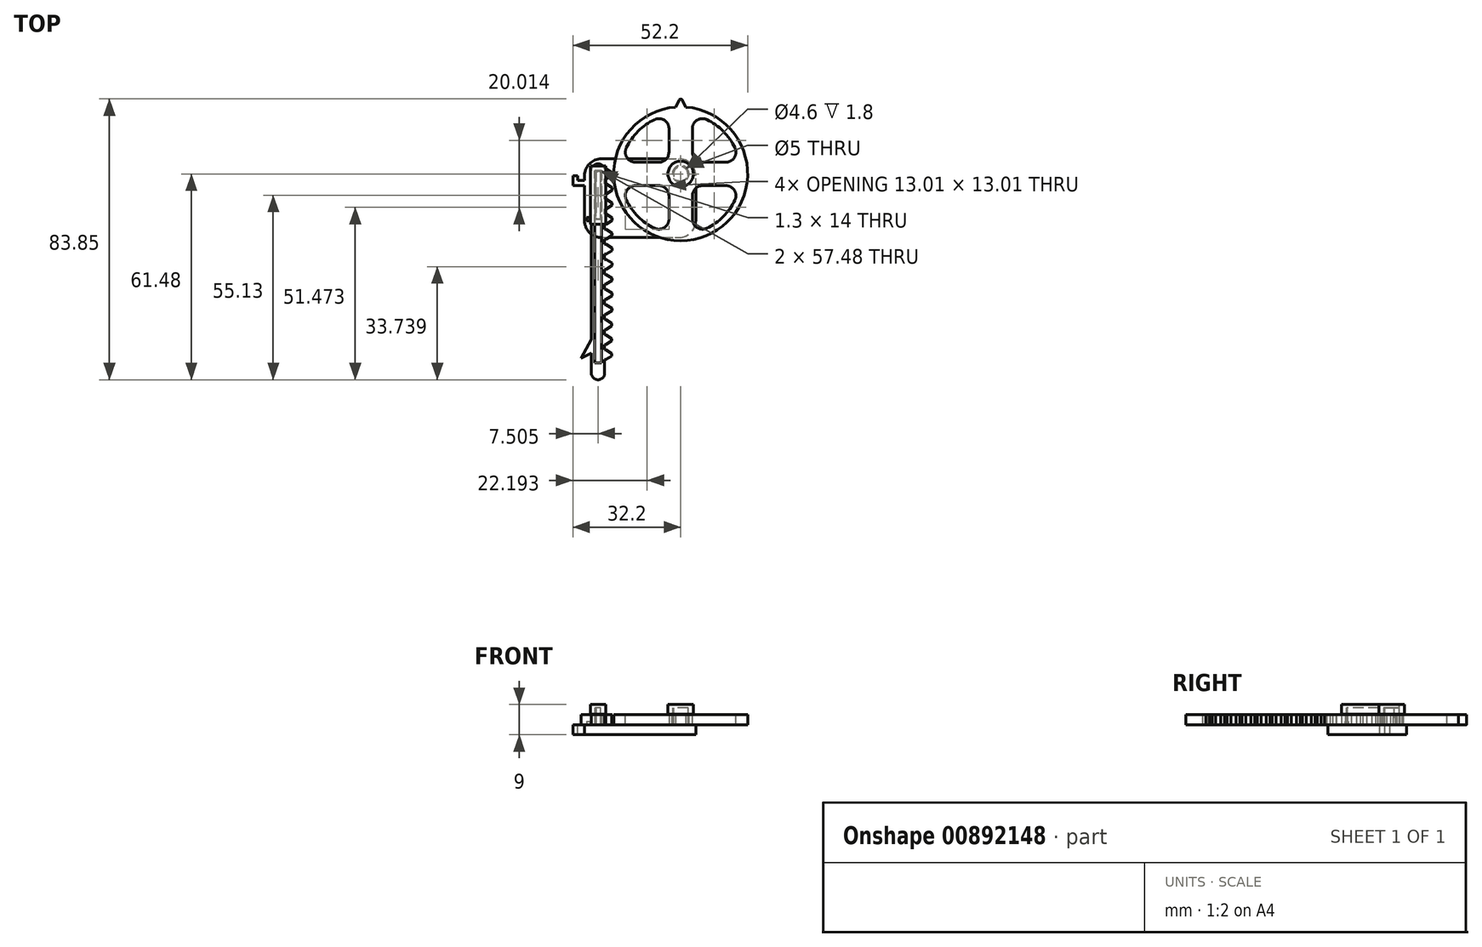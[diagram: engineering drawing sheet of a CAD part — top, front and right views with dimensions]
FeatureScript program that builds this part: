
annotation { "Feature Type Name" : "Feature", "Feature Type Description" : "" }
export const myFeature = defineFeature(function(context is Context, id is Id, definition is map)
    precondition{}
    {
        {
            var Q0;
            Q0=qCreatedBy(makeId("Top.planeOp"),FACE);
            var sketch = newSketch(context, id + "F0", { "sketchPlane" : qUnion([Q0])});
            skCircle(sketch, "E0", {"center": v(0, 0) * mm, "radius": 20 * mm});
            skLineSegment(sketch, "E1", {"start": v(-1.5, 19.94) * mm, "end": v(0, 23) * mm});
            skLineSegment(sketch, "E2", {"start": v(0, 23) * mm, "end": v(1.5, 19.94) * mm});
            skSolve(sketch);
        }
        {
            var Q0;
            {var subQ0=sQuery(id+"F0.wireOp",EDGE,"E0");var subQ1=makeQuery(id+"F0.imprint","INTERSECT",VERTEX,{"derivedFrom":[subQ0,sQuery(id+"F0.wireOp",EDGE,"E1")]});Q0=makeQuery(id+"F0.imprint","IMPRINT",FACE,{"disambiguationData":[TD([[makeQuery(id+"F0.imprint","IMPRINT",EDGE,{"disambiguationData":[TD([[subQ1,1.0]])],"derivedFrom":subQ0}),1.0]])]});}
            extrude(context, id + "F1", {"entities" : qUnion([Q0]), "depth" : 3 * mm, "offsetDistance" : 25 * mm});
        }
        {
            var Q0;
            {var subQ0=sQuery(id+"F0.wireOp",EDGE,"E1");Q0=makeQuery(id+"F0.imprint","IMPRINT",FACE,{"disambiguationData":[TD([[makeQuery(id+"F0.imprint","IMPRINT",EDGE,{"derivedFrom":subQ0}),-1.0]])]});}
            extrude(context, id + "F2", {"entities" : qUnion([Q0]), "operationType" : NewBodyOperationType.ADD, "depth" : 3 * mm, "offsetDistance" : 25 * mm});
        }
        {
            var Q0;
            Q0=makeQuery(id+"F2.opExtrude","SWEPT_EDGE",EDGE,{"disambiguationData":[OSD([sQuery(id+"F0.wireOp",EDGE,"E1"),sQuery(id+"F0.wireOp",EDGE,"E2")])]});
            fillet(context, id + "F3", {"entities" : qUnion([Q0]), "radius" : .5 * mm, "tangentPropagation" : true, "allowEdgeOverflow" : false});
        }
        {
            var Q0;
            Q0=qCreatedBy(makeId("Top.planeOp"),FACE);
            var sketch = newSketch(context, id + "F4", { "sketchPlane" : qUnion([Q0])});
            skLineSegment(sketch, "E3.bottom", {"start": v(-26.7, -61.48) * mm, "end": v(-22.7, -61.48) * mm});
            skLineSegment(sketch, "E3.top", {"start": v(-26.7, 3) * mm, "end": v(-22.7, 3) * mm});
            skLineSegment(sketch, "E3.left", {"start": v(-26.7, -61.48) * mm, "end": v(-26.7, 3) * mm});
            skLineSegment(sketch, "E3.right", {"start": v(-22.7, -61.48) * mm, "end": v(-22.7, 3) * mm});
            skLineSegment(sketch, "E4.117", {"start": v(-22.25, -1.48) * mm, "end": v(-20.45, -0.35) * mm});
            skArc(sketch, "E4.118", {"start": v(-20.45, -0.35) * mm, "mid": v(-20.45, 0) * mm, "end": v(-20.45, 0.35) * mm});
            skLineSegment(sketch, "E4.119", {"start": v(-20.45, 0.35) * mm, "end": v(-22.25, 1.48) * mm});
            skLineSegment(sketch, "E5", {"start": v(-22.25, -1.48) * mm, "end": v(-22.7, -1.48) * mm});
            skLineSegment(sketch, "E6", {"start": v(-22.25, 1.48) * mm, "end": v(-22.7, 1.48) * mm});
            skLineSegment(sketch, "E7.1.0.0", {"start": v(-22.26, -5.98) * mm, "end": v(-22.7, -5.98) * mm});
            skLineSegment(sketch, "E7.1.0.1", {"start": v(-20.46, -4.15) * mm, "end": v(-22.26, -3.02) * mm});
            skArc(sketch, "E7.1.0.2", {"start": v(-20.46, -4.85) * mm, "mid": v(-20.46, -4.5) * mm, "end": v(-20.46, -4.15) * mm});
            skLineSegment(sketch, "E7.1.0.3", {"start": v(-22.26, -3.02) * mm, "end": v(-22.7, -3.02) * mm});
            skLineSegment(sketch, "E7.1.0.4", {"start": v(-22.26, -5.98) * mm, "end": v(-20.46, -4.85) * mm});
            skLineSegment(sketch, "E7.2.0.0", {"start": v(-22.27, -10.48) * mm, "end": v(-22.71, -10.48) * mm});
            skLineSegment(sketch, "E7.2.0.1", {"start": v(-20.46, -8.65) * mm, "end": v(-22.27, -7.52) * mm});
            skArc(sketch, "E7.2.0.2", {"start": v(-20.46, -9.35) * mm, "mid": v(-20.47, -9) * mm, "end": v(-20.46, -8.65) * mm});
            skLineSegment(sketch, "E7.2.0.3", {"start": v(-22.27, -7.52) * mm, "end": v(-22.71, -7.52) * mm});
            skLineSegment(sketch, "E7.2.0.4", {"start": v(-22.27, -10.48) * mm, "end": v(-20.46, -9.35) * mm});
            skLineSegment(sketch, "E7.3.0.0", {"start": v(-22.27, -14.98) * mm, "end": v(-22.72, -14.98) * mm});
            skLineSegment(sketch, "E7.3.0.1", {"start": v(-20.47, -13.15) * mm, "end": v(-22.27, -12.02) * mm});
            skArc(sketch, "E7.3.0.2", {"start": v(-20.47, -13.85) * mm, "mid": v(-20.47, -13.5) * mm, "end": v(-20.47, -13.15) * mm});
            skLineSegment(sketch, "E7.3.0.3", {"start": v(-22.27, -12.02) * mm, "end": v(-22.72, -12.02) * mm});
            skLineSegment(sketch, "E7.3.0.4", {"start": v(-22.27, -14.98) * mm, "end": v(-20.47, -13.85) * mm});
            skLineSegment(sketch, "E7.4.0.0", {"start": v(-22.28, -19.48) * mm, "end": v(-22.73, -19.48) * mm});
            skLineSegment(sketch, "E7.4.0.1", {"start": v(-20.48, -17.65) * mm, "end": v(-22.28, -16.52) * mm});
            skArc(sketch, "E7.4.0.2", {"start": v(-20.48, -18.35) * mm, "mid": v(-20.48, -18) * mm, "end": v(-20.48, -17.65) * mm});
            skLineSegment(sketch, "E7.4.0.3", {"start": v(-22.28, -16.52) * mm, "end": v(-22.73, -16.52) * mm});
            skLineSegment(sketch, "E7.4.0.4", {"start": v(-22.28, -19.48) * mm, "end": v(-20.48, -18.35) * mm});
            skLineSegment(sketch, "E7.5.0.0", {"start": v(-22.3, -23.98) * mm, "end": v(-22.74, -23.98) * mm});
            skLineSegment(sketch, "E7.5.0.1", {"start": v(-20.49, -22.15) * mm, "end": v(-22.3, -21.02) * mm});
            skArc(sketch, "E7.5.0.2", {"start": v(-20.49, -22.85) * mm, "mid": v(-20.5, -22.5) * mm, "end": v(-20.49, -22.15) * mm});
            skLineSegment(sketch, "E7.5.0.3", {"start": v(-22.3, -21.02) * mm, "end": v(-22.74, -21.02) * mm});
            skLineSegment(sketch, "E7.5.0.4", {"start": v(-22.3, -23.98) * mm, "end": v(-20.49, -22.85) * mm});
            skLineSegment(sketch, "E7.6.0.0", {"start": v(-22.3, -28.48) * mm, "end": v(-22.74, -28.48) * mm});
            skLineSegment(sketch, "E7.6.0.1", {"start": v(-20.5, -26.65) * mm, "end": v(-22.3, -25.52) * mm});
            skArc(sketch, "E7.6.0.2", {"start": v(-20.5, -27.35) * mm, "mid": v(-20.5, -27) * mm, "end": v(-20.5, -26.65) * mm});
            skLineSegment(sketch, "E7.6.0.3", {"start": v(-22.3, -25.52) * mm, "end": v(-22.74, -25.52) * mm});
            skLineSegment(sketch, "E7.6.0.4", {"start": v(-22.3, -28.48) * mm, "end": v(-20.5, -27.35) * mm});
            skLineSegment(sketch, "E7.7.0.0", {"start": v(-22.3, -32.98) * mm, "end": v(-22.75, -32.98) * mm});
            skLineSegment(sketch, "E7.7.0.1", {"start": v(-20.5, -31.15) * mm, "end": v(-22.3, -30.02) * mm});
            skArc(sketch, "E7.7.0.2", {"start": v(-20.5, -31.85) * mm, "mid": v(-20.5, -31.5) * mm, "end": v(-20.5, -31.15) * mm});
            skLineSegment(sketch, "E7.7.0.3", {"start": v(-22.3, -30.02) * mm, "end": v(-22.75, -30.02) * mm});
            skLineSegment(sketch, "E7.7.0.4", {"start": v(-22.3, -32.98) * mm, "end": v(-20.5, -31.85) * mm});
            skLineSegment(sketch, "E7.8.0.0", {"start": v(-22.32, -37.48) * mm, "end": v(-22.76, -37.48) * mm});
            skLineSegment(sketch, "E7.8.0.1", {"start": v(-20.51, -35.65) * mm, "end": v(-22.32, -34.52) * mm});
            skArc(sketch, "E7.8.0.2", {"start": v(-20.51, -36.35) * mm, "mid": v(-20.51, -36) * mm, "end": v(-20.51, -35.65) * mm});
            skLineSegment(sketch, "E7.8.0.3", {"start": v(-22.32, -34.52) * mm, "end": v(-22.76, -34.52) * mm});
            skLineSegment(sketch, "E7.8.0.4", {"start": v(-22.32, -37.48) * mm, "end": v(-20.51, -36.35) * mm});
            skLineSegment(sketch, "E7.9.0.0", {"start": v(-22.32, -41.98) * mm, "end": v(-22.77, -41.98) * mm});
            skLineSegment(sketch, "E7.9.0.1", {"start": v(-20.52, -40.15) * mm, "end": v(-22.32, -39.02) * mm});
            skArc(sketch, "E7.9.0.2", {"start": v(-20.52, -40.85) * mm, "mid": v(-20.52, -40.5) * mm, "end": v(-20.52, -40.15) * mm});
            skLineSegment(sketch, "E7.9.0.3", {"start": v(-22.32, -39.02) * mm, "end": v(-22.77, -39.02) * mm});
            skLineSegment(sketch, "E7.9.0.4", {"start": v(-22.32, -41.98) * mm, "end": v(-20.52, -40.85) * mm});
            skLineSegment(sketch, "E7.10.0.0", {"start": v(-22.33, -46.48) * mm, "end": v(-22.78, -46.48) * mm});
            skLineSegment(sketch, "E7.10.0.1", {"start": v(-20.53, -44.65) * mm, "end": v(-22.33, -43.52) * mm});
            skArc(sketch, "E7.10.0.2", {"start": v(-20.53, -45.35) * mm, "mid": v(-20.53, -45) * mm, "end": v(-20.53, -44.65) * mm});
            skLineSegment(sketch, "E7.10.0.3", {"start": v(-22.33, -43.52) * mm, "end": v(-22.78, -43.52) * mm});
            skLineSegment(sketch, "E7.10.0.4", {"start": v(-22.33, -46.48) * mm, "end": v(-20.53, -45.35) * mm});
            skLineSegment(sketch, "E7.11.0.0", {"start": v(-22.34, -50.98) * mm, "end": v(-22.78, -50.98) * mm});
            skLineSegment(sketch, "E7.11.0.1", {"start": v(-20.54, -49.15) * mm, "end": v(-22.34, -48.02) * mm});
            skArc(sketch, "E7.11.0.2", {"start": v(-20.54, -49.85) * mm, "mid": v(-20.54, -49.5) * mm, "end": v(-20.54, -49.15) * mm});
            skLineSegment(sketch, "E7.11.0.3", {"start": v(-22.34, -48.02) * mm, "end": v(-22.78, -48.02) * mm});
            skLineSegment(sketch, "E7.11.0.4", {"start": v(-22.34, -50.98) * mm, "end": v(-20.54, -49.85) * mm});
            skLineSegment(sketch, "E7.12.0.0", {"start": v(-22.35, -55.48) * mm, "end": v(-22.8, -55.48) * mm});
            skLineSegment(sketch, "E7.12.0.1", {"start": v(-20.54, -53.65) * mm, "end": v(-22.35, -52.52) * mm});
            skArc(sketch, "E7.12.0.2", {"start": v(-20.54, -54.35) * mm, "mid": v(-20.55, -54) * mm, "end": v(-20.54, -53.65) * mm});
            skLineSegment(sketch, "E7.12.0.3", {"start": v(-22.35, -52.52) * mm, "end": v(-22.8, -52.52) * mm});
            skLineSegment(sketch, "E7.12.0.4", {"start": v(-22.35, -55.48) * mm, "end": v(-20.54, -54.35) * mm});
            skLineSegment(sketch, "E7.direction1", {"start": v(-22.7, -1.48) * mm, "end": v(-22.7, -5.98) * mm, "construction": true});
            skSolve(sketch);
        }
        {
            var Q0;
            Q0 = qSketchRegion(id + "F4", true);
            extrude(context, id + "F5", {"entities" : qUnion([Q0]), "depth" : 3 * mm, "offsetDistance" : 25 * mm});
        }
        {
            var Q0;
            Q0=makeQuery(id+"F5.opExtrude","CAP_FACE",FACE,{"disambiguationData":[OSD([sQuery(id+"F4.wireOp",EDGE,"E3.bottom"),sQuery(id+"F4.wireOp",EDGE,"E3.top"),sQuery(id+"F4.wireOp",EDGE,"E3.left"),sQuery(id+"F4.wireOp",EDGE,"E3.right"),sQuery(id+"F4.wireOp",EDGE,"E4.117"),sQuery(id+"F4.wireOp",EDGE,"E4.118"),sQuery(id+"F4.wireOp",EDGE,"E4.119"),sQuery(id+"F4.wireOp",EDGE,"E5"),sQuery(id+"F4.wireOp",EDGE,"E6"),sQuery(id+"F4.wireOp",EDGE,"E7.1.0.0"),sQuery(id+"F4.wireOp",EDGE,"E7.1.0.1"),sQuery(id+"F4.wireOp",EDGE,"E7.1.0.2"),sQuery(id+"F4.wireOp",EDGE,"E7.1.0.3"),sQuery(id+"F4.wireOp",EDGE,"E7.1.0.4"),sQuery(id+"F4.wireOp",EDGE,"E7.2.0.0"),sQuery(id+"F4.wireOp",EDGE,"E7.2.0.1"),sQuery(id+"F4.wireOp",EDGE,"E7.2.0.2"),sQuery(id+"F4.wireOp",EDGE,"E7.2.0.3"),sQuery(id+"F4.wireOp",EDGE,"E7.2.0.4"),sQuery(id+"F4.wireOp",EDGE,"E7.3.0.0"),sQuery(id+"F4.wireOp",EDGE,"E7.3.0.1"),sQuery(id+"F4.wireOp",EDGE,"E7.3.0.2"),sQuery(id+"F4.wireOp",EDGE,"E7.3.0.3"),sQuery(id+"F4.wireOp",EDGE,"E7.3.0.4"),sQuery(id+"F4.wireOp",EDGE,"E7.4.0.0"),sQuery(id+"F4.wireOp",EDGE,"E7.4.0.1"),sQuery(id+"F4.wireOp",EDGE,"E7.4.0.2"),sQuery(id+"F4.wireOp",EDGE,"E7.4.0.3"),sQuery(id+"F4.wireOp",EDGE,"E7.4.0.4"),sQuery(id+"F4.wireOp",EDGE,"E7.5.0.0"),sQuery(id+"F4.wireOp",EDGE,"E7.5.0.1"),sQuery(id+"F4.wireOp",EDGE,"E7.5.0.2"),sQuery(id+"F4.wireOp",EDGE,"E7.5.0.3"),sQuery(id+"F4.wireOp",EDGE,"E7.5.0.4"),sQuery(id+"F4.wireOp",EDGE,"E7.6.0.0"),sQuery(id+"F4.wireOp",EDGE,"E7.6.0.1"),sQuery(id+"F4.wireOp",EDGE,"E7.6.0.2"),sQuery(id+"F4.wireOp",EDGE,"E7.6.0.3"),sQuery(id+"F4.wireOp",EDGE,"E7.6.0.4"),sQuery(id+"F4.wireOp",EDGE,"E7.7.0.0"),sQuery(id+"F4.wireOp",EDGE,"E7.7.0.1"),sQuery(id+"F4.wireOp",EDGE,"E7.7.0.2"),sQuery(id+"F4.wireOp",EDGE,"E7.7.0.3"),sQuery(id+"F4.wireOp",EDGE,"E7.7.0.4"),sQuery(id+"F4.wireOp",EDGE,"E7.8.0.0"),sQuery(id+"F4.wireOp",EDGE,"E7.8.0.1"),sQuery(id+"F4.wireOp",EDGE,"E7.8.0.2"),sQuery(id+"F4.wireOp",EDGE,"E7.8.0.3"),sQuery(id+"F4.wireOp",EDGE,"E7.8.0.4"),sQuery(id+"F4.wireOp",EDGE,"E7.9.0.0"),sQuery(id+"F4.wireOp",EDGE,"E7.9.0.1"),sQuery(id+"F4.wireOp",EDGE,"E7.9.0.2"),sQuery(id+"F4.wireOp",EDGE,"E7.9.0.3"),sQuery(id+"F4.wireOp",EDGE,"E7.9.0.4"),sQuery(id+"F4.wireOp",EDGE,"E7.10.0.0"),sQuery(id+"F4.wireOp",EDGE,"E7.10.0.1"),sQuery(id+"F4.wireOp",EDGE,"E7.10.0.2"),sQuery(id+"F4.wireOp",EDGE,"E7.10.0.3"),sQuery(id+"F4.wireOp",EDGE,"E7.10.0.4"),sQuery(id+"F4.wireOp",EDGE,"E7.11.0.0"),sQuery(id+"F4.wireOp",EDGE,"E7.11.0.1"),sQuery(id+"F4.wireOp",EDGE,"E7.11.0.2"),sQuery(id+"F4.wireOp",EDGE,"E7.11.0.3"),sQuery(id+"F4.wireOp",EDGE,"E7.11.0.4"),sQuery(id+"F4.wireOp",EDGE,"E7.12.0.0"),sQuery(id+"F4.wireOp",EDGE,"E7.12.0.1"),sQuery(id+"F4.wireOp",EDGE,"E7.12.0.2"),sQuery(id+"F4.wireOp",EDGE,"E7.12.0.3"),sQuery(id+"F4.wireOp",EDGE,"E7.12.0.4")])],"isStart":true});
            var sketch = newSketch(context, id + "F6", { "sketchPlane" : qUnion([Q0])});
            skLineSegment(sketch, "E8.bottom", {"start": v(-25.7, 56.48) * mm, "end": v(-23.7, 56.48) * mm});
            skLineSegment(sketch, "E8.top", {"start": v(-25.7, -1) * mm, "end": v(-23.7, -1) * mm});
            skLineSegment(sketch, "E8.left", {"start": v(-25.7, 56.48) * mm, "end": v(-25.7, -1) * mm});
            skLineSegment(sketch, "E8.right", {"start": v(-23.7, 56.48) * mm, "end": v(-23.7, -1) * mm});
            skSolve(sketch);
        }
        {
            var Q0;
            Q0=makeQuery(id+"F6.imprint","IMPRINT",FACE,{"disambiguationData":[TD([[makeQuery(id+"F6.imprint","IMPRINT",EDGE,{"derivedFrom":sQuery(id+"F6.wireOp",EDGE,"E8.bottom")}),-1.0]])]});
            extrude(context, id + "F7", {"entities" : qUnion([Q0]), "operationType" : NewBodyOperationType.REMOVE, "endBound" : BoundingType.THROUGH_ALL, "oppositeDirection" : true, "depth" : 25 * mm, "offsetDistance" : 25 * mm});
        }
        {
            var Q0;
            Q0=makeQuery(id+"F5.opExtrude","SWEPT_EDGE",EDGE,{"disambiguationData":[OSD([sQuery(id+"F4.wireOp",EDGE,"E3.top"),sQuery(id+"F4.wireOp",EDGE,"E3.right")])]});
            var Q1;
            Q1=makeQuery(id+"F5.opExtrude","SWEPT_EDGE",EDGE,{"disambiguationData":[OSD([sQuery(id+"F4.wireOp",EDGE,"E3.top"),sQuery(id+"F4.wireOp",EDGE,"E3.left")])]});
            var Q2;
            Q2=makeQuery(id+"F5.opExtrude","SWEPT_EDGE",EDGE,{"disambiguationData":[OSD([sQuery(id+"F4.wireOp",EDGE,"E3.bottom"),sQuery(id+"F4.wireOp",EDGE,"E3.left")])]});
            var Q3;
            Q3=makeQuery(id+"F5.opExtrude","SWEPT_EDGE",EDGE,{"disambiguationData":[OSD([sQuery(id+"F4.wireOp",EDGE,"E3.bottom"),sQuery(id+"F4.wireOp",EDGE,"E3.right")])]});
            fillet(context, id + "F8", {"entities" : qUnion([Q0, Q1, Q2, Q3]), "radius" : 2 * mm, "tangentPropagation" : true, "allowEdgeOverflow" : false});
        }
        {
            var Q0;
            {var subQ0=sQuery(id+"F0.wireOp",EDGE,"E2");var subQ1=sQuery(id+"F0.wireOp",EDGE,"E1");var subQ2=sQuery(id+"F0.wireOp",EDGE,"E0");Q0=makeQuery(id+"FbRMCi4XYvqGRgo_1.29.F2.boolean.opBoolean","MERGE",FACE,{"derivedFrom":[makeQuery(id+"FbRMCi4XYvqGRgo_1.28.F2.boolean.opBoolean","MERGE",FACE,{"derivedFrom":[makeQuery(id+"FbRMCi4XYvqGRgo_1.27.F2.boolean.opBoolean","MERGE",FACE,{"derivedFrom":[makeQuery(id+"FbRMCi4XYvqGRgo_1.26.F2.boolean.opBoolean","MERGE",FACE,{"derivedFrom":[makeQuery(id+"FbRMCi4XYvqGRgo_1.25.F2.boolean.opBoolean","MERGE",FACE,{"derivedFrom":[makeQuery(id+"FbRMCi4XYvqGRgo_1.24.F2.boolean.opBoolean","MERGE",FACE,{"derivedFrom":[makeQuery(id+"FbRMCi4XYvqGRgo_1.23.F2.boolean.opBoolean","MERGE",FACE,{"derivedFrom":[makeQuery(id+"FbRMCi4XYvqGRgo_1.22.F2.boolean.opBoolean","MERGE",FACE,{"derivedFrom":[makeQuery(id+"FbRMCi4XYvqGRgo_1.21.F2.boolean.opBoolean","MERGE",FACE,{"derivedFrom":[makeQuery(id+"FbRMCi4XYvqGRgo_1.20.F2.boolean.opBoolean","MERGE",FACE,{"derivedFrom":[makeQuery(id+"FbRMCi4XYvqGRgo_1.19.F2.boolean.opBoolean","MERGE",FACE,{"derivedFrom":[makeQuery(id+"FbRMCi4XYvqGRgo_1.18.F2.boolean.opBoolean","MERGE",FACE,{"derivedFrom":[makeQuery(id+"FbRMCi4XYvqGRgo_1.17.F2.boolean.opBoolean","MERGE",FACE,{"derivedFrom":[makeQuery(id+"FbRMCi4XYvqGRgo_1.16.F2.boolean.opBoolean","MERGE",FACE,{"derivedFrom":[makeQuery(id+"FbRMCi4XYvqGRgo_1.15.F2.boolean.opBoolean","MERGE",FACE,{"derivedFrom":[makeQuery(id+"FbRMCi4XYvqGRgo_1.14.F2.boolean.opBoolean","MERGE",FACE,{"derivedFrom":[makeQuery(id+"FbRMCi4XYvqGRgo_1.13.F2.boolean.opBoolean","MERGE",FACE,{"derivedFrom":[makeQuery(id+"FbRMCi4XYvqGRgo_1.12.F2.boolean.opBoolean","MERGE",FACE,{"derivedFrom":[makeQuery(id+"FbRMCi4XYvqGRgo_1.11.F2.boolean.opBoolean","MERGE",FACE,{"derivedFrom":[makeQuery(id+"FbRMCi4XYvqGRgo_1.10.F2.boolean.opBoolean","MERGE",FACE,{"derivedFrom":[makeQuery(id+"FbRMCi4XYvqGRgo_1.9.F2.boolean.opBoolean","MERGE",FACE,{"derivedFrom":[makeQuery(id+"FbRMCi4XYvqGRgo_1.8.F2.boolean.opBoolean","MERGE",FACE,{"derivedFrom":[makeQuery(id+"FbRMCi4XYvqGRgo_1.7.F2.boolean.opBoolean","MERGE",FACE,{"derivedFrom":[makeQuery(id+"FbRMCi4XYvqGRgo_1.6.F2.boolean.opBoolean","MERGE",FACE,{"derivedFrom":[makeQuery(id+"FbRMCi4XYvqGRgo_1.5.F2.boolean.opBoolean","MERGE",FACE,{"derivedFrom":[makeQuery(id+"FbRMCi4XYvqGRgo_1.4.F2.boolean.opBoolean","MERGE",FACE,{"derivedFrom":[makeQuery(id+"FbRMCi4XYvqGRgo_1.3.F2.boolean.opBoolean","MERGE",FACE,{"derivedFrom":[makeQuery(id+"FbRMCi4XYvqGRgo_1.2.F2.boolean.opBoolean","MERGE",FACE,{"derivedFrom":[makeQuery(id+"FbRMCi4XYvqGRgo_1.1.F2.boolean.opBoolean","MERGE",FACE,{"derivedFrom":[makeQuery(id+"F2.boolean.opBoolean","MERGE",FACE,{"derivedFrom":[makeQuery(id+"F1.opExtrude","CAP_FACE",FACE,{"disambiguationData":[OSD([subQ2])],"isStart":false}),makeQuery(id+"F2.opExtrude","CAP_FACE",FACE,{"disambiguationData":[OSD([subQ2,subQ1,subQ0])],"isStart":false})]}),makeQuery(id+"FbRMCi4XYvqGRgo_1.1.F2.opExtrude","CAP_FACE",FACE,{"disambiguationData":[OSD([subQ2,subQ1,subQ0])],"isStart":false})]}),makeQuery(id+"FbRMCi4XYvqGRgo_1.2.F2.opExtrude","CAP_FACE",FACE,{"disambiguationData":[OSD([subQ2,subQ1,subQ0])],"isStart":false})]}),makeQuery(id+"FbRMCi4XYvqGRgo_1.3.F2.opExtrude","CAP_FACE",FACE,{"disambiguationData":[OSD([subQ2,subQ1,subQ0])],"isStart":false})]}),makeQuery(id+"FbRMCi4XYvqGRgo_1.4.F2.opExtrude","CAP_FACE",FACE,{"disambiguationData":[OSD([subQ2,subQ1,subQ0])],"isStart":false})]}),makeQuery(id+"FbRMCi4XYvqGRgo_1.5.F2.opExtrude","CAP_FACE",FACE,{"disambiguationData":[OSD([subQ2,subQ1,subQ0])],"isStart":false})]}),makeQuery(id+"FbRMCi4XYvqGRgo_1.6.F2.opExtrude","CAP_FACE",FACE,{"disambiguationData":[OSD([subQ2,subQ1,subQ0])],"isStart":false})]}),makeQuery(id+"FbRMCi4XYvqGRgo_1.7.F2.opExtrude","CAP_FACE",FACE,{"disambiguationData":[OSD([subQ2,subQ1,subQ0])],"isStart":false})]}),makeQuery(id+"FbRMCi4XYvqGRgo_1.8.F2.opExtrude","CAP_FACE",FACE,{"disambiguationData":[OSD([subQ2,subQ1,subQ0])],"isStart":false})]}),makeQuery(id+"FbRMCi4XYvqGRgo_1.9.F2.opExtrude","CAP_FACE",FACE,{"disambiguationData":[OSD([subQ2,subQ1,subQ0])],"isStart":false})]}),makeQuery(id+"FbRMCi4XYvqGRgo_1.10.F2.opExtrude","CAP_FACE",FACE,{"disambiguationData":[OSD([subQ2,subQ1,subQ0])],"isStart":false})]}),makeQuery(id+"FbRMCi4XYvqGRgo_1.11.F2.opExtrude","CAP_FACE",FACE,{"disambiguationData":[OSD([subQ2,subQ1,subQ0])],"isStart":false})]}),makeQuery(id+"FbRMCi4XYvqGRgo_1.12.F2.opExtrude","CAP_FACE",FACE,{"disambiguationData":[OSD([subQ2,subQ1,subQ0])],"isStart":false})]}),makeQuery(id+"FbRMCi4XYvqGRgo_1.13.F2.opExtrude","CAP_FACE",FACE,{"disambiguationData":[OSD([subQ2,subQ1,subQ0])],"isStart":false})]}),makeQuery(id+"FbRMCi4XYvqGRgo_1.14.F2.opExtrude","CAP_FACE",FACE,{"disambiguationData":[OSD([subQ2,subQ1,subQ0])],"isStart":false})]}),makeQuery(id+"FbRMCi4XYvqGRgo_1.15.F2.opExtrude","CAP_FACE",FACE,{"disambiguationData":[OSD([subQ2,subQ1,subQ0])],"isStart":false})]}),makeQuery(id+"FbRMCi4XYvqGRgo_1.16.F2.opExtrude","CAP_FACE",FACE,{"disambiguationData":[OSD([subQ2,subQ1,subQ0])],"isStart":false})]}),makeQuery(id+"FbRMCi4XYvqGRgo_1.17.F2.opExtrude","CAP_FACE",FACE,{"disambiguationData":[OSD([subQ2,subQ1,subQ0])],"isStart":false})]}),makeQuery(id+"FbRMCi4XYvqGRgo_1.18.F2.opExtrude","CAP_FACE",FACE,{"disambiguationData":[OSD([subQ2,subQ1,subQ0])],"isStart":false})]}),makeQuery(id+"FbRMCi4XYvqGRgo_1.19.F2.opExtrude","CAP_FACE",FACE,{"disambiguationData":[OSD([subQ2,subQ1,subQ0])],"isStart":false})]}),makeQuery(id+"FbRMCi4XYvqGRgo_1.20.F2.opExtrude","CAP_FACE",FACE,{"disambiguationData":[OSD([subQ2,subQ1,subQ0])],"isStart":false})]}),makeQuery(id+"FbRMCi4XYvqGRgo_1.21.F2.opExtrude","CAP_FACE",FACE,{"disambiguationData":[OSD([subQ2,subQ1,subQ0])],"isStart":false})]}),makeQuery(id+"FbRMCi4XYvqGRgo_1.22.F2.opExtrude","CAP_FACE",FACE,{"disambiguationData":[OSD([subQ2,subQ1,subQ0])],"isStart":false})]}),makeQuery(id+"FbRMCi4XYvqGRgo_1.23.F2.opExtrude","CAP_FACE",FACE,{"disambiguationData":[OSD([subQ2,subQ1,subQ0])],"isStart":false})]}),makeQuery(id+"FbRMCi4XYvqGRgo_1.24.F2.opExtrude","CAP_FACE",FACE,{"disambiguationData":[OSD([subQ2,subQ1,subQ0])],"isStart":false})]}),makeQuery(id+"FbRMCi4XYvqGRgo_1.25.F2.opExtrude","CAP_FACE",FACE,{"disambiguationData":[OSD([subQ2,subQ1,subQ0])],"isStart":false})]}),makeQuery(id+"FbRMCi4XYvqGRgo_1.26.F2.opExtrude","CAP_FACE",FACE,{"disambiguationData":[OSD([subQ2,subQ1,subQ0])],"isStart":false})]}),makeQuery(id+"FbRMCi4XYvqGRgo_1.27.F2.opExtrude","CAP_FACE",FACE,{"disambiguationData":[OSD([subQ2,subQ1,subQ0])],"isStart":false})]}),makeQuery(id+"FbRMCi4XYvqGRgo_1.28.F2.opExtrude","CAP_FACE",FACE,{"disambiguationData":[OSD([subQ2,subQ1,subQ0])],"isStart":false})]}),makeQuery(id+"FbRMCi4XYvqGRgo_1.29.F2.opExtrude","CAP_FACE",FACE,{"disambiguationData":[OSD([subQ2,subQ1,subQ0])],"isStart":false})]});}
            var sketch = newSketch(context, id + "F9", { "sketchPlane" : qUnion([Q0])});
            skCircle(sketch, "E9", {"center": v(0, 0) * mm, "radius": 18 * mm});
            skSolve(sketch);
        }
        {
            var Q0;
            Q0=makeQuery(id+"F9.imprint","IMPRINT",FACE,{"disambiguationData":[TD([[makeQuery(id+"F9.imprint","IMPRINT",EDGE,{"derivedFrom":sQuery(id+"F9.wireOp",EDGE,"E9")}),1.0]])]});
            extrude(context, id + "F10", {"entities" : qUnion([Q0]), "operationType" : NewBodyOperationType.REMOVE, "endBound" : BoundingType.THROUGH_ALL, "oppositeDirection" : true, "depth" : 25 * mm, "offsetDistance" : 25 * mm});
        }
        {
            var Q0;
            Q0=qCreatedBy(makeId("Top.planeOp"),FACE);
            var sketch = newSketch(context, id + "F11", { "sketchPlane" : qUnion([Q0])});
            skLineSegment(sketch, "E10.bottom", {"start": v(-3.5, 18.5) * mm, "end": v(3.5, 18.5) * mm});
            skLineSegment(sketch, "E10.top", {"start": v(-3.5, -18.5) * mm, "end": v(3.5, -18.5) * mm});
            skLineSegment(sketch, "E10.left", {"start": v(-3.5, 18.5) * mm, "end": v(-3.5, -18.5) * mm});
            skLineSegment(sketch, "E10.right", {"start": v(3.5, 18.5) * mm, "end": v(3.5, -18.5) * mm});
            skPoint(sketch, "E10.middle", {"position": v(0, 0) * mm});
            skLineSegment(sketch, "E11.bottom", {"start": v(-18.5, 3.5) * mm, "end": v(18.5, 3.5) * mm});
            skLineSegment(sketch, "E11.top", {"start": v(-18.5, -3.5) * mm, "end": v(18.5, -3.5) * mm});
            skLineSegment(sketch, "E11.left", {"start": v(-18.5, 3.5) * mm, "end": v(-18.5, -3.5) * mm});
            skLineSegment(sketch, "E11.right", {"start": v(18.5, 3.5) * mm, "end": v(18.5, -3.5) * mm});
            skSolve(sketch);
        }
        {
            var Q0;
            {var subQ5=sQuery(id+"F11.wireOp",EDGE,"E11.left");Q0=makeQuery(id+"F11.imprint","IMPRINT",FACE,{"disambiguationData":[TD([[makeQuery(id+"F11.imprint","IMPRINT",EDGE,{"derivedFrom":subQ5}),1.0]])]});}
            var Q1;
            {var subQ0=sQuery(id+"F11.wireOp",EDGE,"E10.bottom");Q1=makeQuery(id+"F11.imprint","IMPRINT",FACE,{"disambiguationData":[TD([[makeQuery(id+"F11.imprint","IMPRINT",EDGE,{"derivedFrom":subQ0}),-1.0]])]});}
            var Q2;
            {var subQ0=sQuery(id+"F11.wireOp",EDGE,"E11.bottom");var subQ1=sQuery(id+"F11.wireOp",EDGE,"E10.left");var subQ2=makeQuery(id+"F11.imprint","INTERSECT",VERTEX,{"derivedFrom":[subQ1,subQ0]});Q2=makeQuery(id+"F11.imprint","IMPRINT",FACE,{"disambiguationData":[TD([[makeQuery(id+"F11.imprint","IMPRINT",EDGE,{"disambiguationData":[TD([[subQ2,-1.0]])],"derivedFrom":subQ1}),1.0]])]});}
            var Q3;
            {var subQ0=sQuery(id+"F11.wireOp",EDGE,"E10.top");Q3=makeQuery(id+"F11.imprint","IMPRINT",FACE,{"disambiguationData":[TD([[makeQuery(id+"F11.imprint","IMPRINT",EDGE,{"derivedFrom":subQ0}),1.0]])]});}
            var Q4;
            {var subQ5=sQuery(id+"F11.wireOp",EDGE,"E11.right");Q4=makeQuery(id+"F11.imprint","IMPRINT",FACE,{"disambiguationData":[TD([[makeQuery(id+"F11.imprint","IMPRINT",EDGE,{"derivedFrom":subQ5}),-1.0]])]});}
            extrude(context, id + "F12", {"entities" : qUnion([Q0, Q1, Q2, Q3, Q4]), "operationType" : NewBodyOperationType.ADD, "depth" : 3 * mm, "offsetDistance" : 25 * mm});
        }
        {
            var Q0;
            {var subQ0=sQuery(id+"F0.wireOp",EDGE,"E2");var subQ1=sQuery(id+"F0.wireOp",EDGE,"E1");var subQ2=sQuery(id+"F0.wireOp",EDGE,"E0");Q0=makeQuery(id+"F12.boolean.opBoolean","MERGE",FACE,{"derivedFrom":[makeQuery(id+"FbRMCi4XYvqGRgo_1.29.F2.boolean.opBoolean","MERGE",FACE,{"derivedFrom":[makeQuery(id+"FbRMCi4XYvqGRgo_1.28.F2.boolean.opBoolean","MERGE",FACE,{"derivedFrom":[makeQuery(id+"FbRMCi4XYvqGRgo_1.27.F2.boolean.opBoolean","MERGE",FACE,{"derivedFrom":[makeQuery(id+"FbRMCi4XYvqGRgo_1.26.F2.boolean.opBoolean","MERGE",FACE,{"derivedFrom":[makeQuery(id+"FbRMCi4XYvqGRgo_1.25.F2.boolean.opBoolean","MERGE",FACE,{"derivedFrom":[makeQuery(id+"FbRMCi4XYvqGRgo_1.24.F2.boolean.opBoolean","MERGE",FACE,{"derivedFrom":[makeQuery(id+"FbRMCi4XYvqGRgo_1.23.F2.boolean.opBoolean","MERGE",FACE,{"derivedFrom":[makeQuery(id+"FbRMCi4XYvqGRgo_1.22.F2.boolean.opBoolean","MERGE",FACE,{"derivedFrom":[makeQuery(id+"FbRMCi4XYvqGRgo_1.21.F2.boolean.opBoolean","MERGE",FACE,{"derivedFrom":[makeQuery(id+"FbRMCi4XYvqGRgo_1.20.F2.boolean.opBoolean","MERGE",FACE,{"derivedFrom":[makeQuery(id+"FbRMCi4XYvqGRgo_1.19.F2.boolean.opBoolean","MERGE",FACE,{"derivedFrom":[makeQuery(id+"FbRMCi4XYvqGRgo_1.18.F2.boolean.opBoolean","MERGE",FACE,{"derivedFrom":[makeQuery(id+"FbRMCi4XYvqGRgo_1.17.F2.boolean.opBoolean","MERGE",FACE,{"derivedFrom":[makeQuery(id+"FbRMCi4XYvqGRgo_1.16.F2.boolean.opBoolean","MERGE",FACE,{"derivedFrom":[makeQuery(id+"FbRMCi4XYvqGRgo_1.15.F2.boolean.opBoolean","MERGE",FACE,{"derivedFrom":[makeQuery(id+"FbRMCi4XYvqGRgo_1.14.F2.boolean.opBoolean","MERGE",FACE,{"derivedFrom":[makeQuery(id+"FbRMCi4XYvqGRgo_1.13.F2.boolean.opBoolean","MERGE",FACE,{"derivedFrom":[makeQuery(id+"FbRMCi4XYvqGRgo_1.12.F2.boolean.opBoolean","MERGE",FACE,{"derivedFrom":[makeQuery(id+"FbRMCi4XYvqGRgo_1.11.F2.boolean.opBoolean","MERGE",FACE,{"derivedFrom":[makeQuery(id+"FbRMCi4XYvqGRgo_1.10.F2.boolean.opBoolean","MERGE",FACE,{"derivedFrom":[makeQuery(id+"FbRMCi4XYvqGRgo_1.9.F2.boolean.opBoolean","MERGE",FACE,{"derivedFrom":[makeQuery(id+"FbRMCi4XYvqGRgo_1.8.F2.boolean.opBoolean","MERGE",FACE,{"derivedFrom":[makeQuery(id+"FbRMCi4XYvqGRgo_1.7.F2.boolean.opBoolean","MERGE",FACE,{"derivedFrom":[makeQuery(id+"FbRMCi4XYvqGRgo_1.6.F2.boolean.opBoolean","MERGE",FACE,{"derivedFrom":[makeQuery(id+"FbRMCi4XYvqGRgo_1.5.F2.boolean.opBoolean","MERGE",FACE,{"derivedFrom":[makeQuery(id+"FbRMCi4XYvqGRgo_1.4.F2.boolean.opBoolean","MERGE",FACE,{"derivedFrom":[makeQuery(id+"FbRMCi4XYvqGRgo_1.3.F2.boolean.opBoolean","MERGE",FACE,{"derivedFrom":[makeQuery(id+"FbRMCi4XYvqGRgo_1.2.F2.boolean.opBoolean","MERGE",FACE,{"derivedFrom":[makeQuery(id+"FbRMCi4XYvqGRgo_1.1.F2.boolean.opBoolean","MERGE",FACE,{"derivedFrom":[makeQuery(id+"F2.boolean.opBoolean","MERGE",FACE,{"derivedFrom":[makeQuery(id+"F1.opExtrude","CAP_FACE",FACE,{"disambiguationData":[OSD([subQ2])],"isStart":false}),makeQuery(id+"F2.opExtrude","CAP_FACE",FACE,{"disambiguationData":[OSD([subQ2,subQ1,subQ0])],"isStart":false})]}),makeQuery(id+"FbRMCi4XYvqGRgo_1.1.F2.opExtrude","CAP_FACE",FACE,{"disambiguationData":[OSD([subQ2,subQ1,subQ0])],"isStart":false})]}),makeQuery(id+"FbRMCi4XYvqGRgo_1.2.F2.opExtrude","CAP_FACE",FACE,{"disambiguationData":[OSD([subQ2,subQ1,subQ0])],"isStart":false})]}),makeQuery(id+"FbRMCi4XYvqGRgo_1.3.F2.opExtrude","CAP_FACE",FACE,{"disambiguationData":[OSD([subQ2,subQ1,subQ0])],"isStart":false})]}),makeQuery(id+"FbRMCi4XYvqGRgo_1.4.F2.opExtrude","CAP_FACE",FACE,{"disambiguationData":[OSD([subQ2,subQ1,subQ0])],"isStart":false})]}),makeQuery(id+"FbRMCi4XYvqGRgo_1.5.F2.opExtrude","CAP_FACE",FACE,{"disambiguationData":[OSD([subQ2,subQ1,subQ0])],"isStart":false})]}),makeQuery(id+"FbRMCi4XYvqGRgo_1.6.F2.opExtrude","CAP_FACE",FACE,{"disambiguationData":[OSD([subQ2,subQ1,subQ0])],"isStart":false})]}),makeQuery(id+"FbRMCi4XYvqGRgo_1.7.F2.opExtrude","CAP_FACE",FACE,{"disambiguationData":[OSD([subQ2,subQ1,subQ0])],"isStart":false})]}),makeQuery(id+"FbRMCi4XYvqGRgo_1.8.F2.opExtrude","CAP_FACE",FACE,{"disambiguationData":[OSD([subQ2,subQ1,subQ0])],"isStart":false})]}),makeQuery(id+"FbRMCi4XYvqGRgo_1.9.F2.opExtrude","CAP_FACE",FACE,{"disambiguationData":[OSD([subQ2,subQ1,subQ0])],"isStart":false})]}),makeQuery(id+"FbRMCi4XYvqGRgo_1.10.F2.opExtrude","CAP_FACE",FACE,{"disambiguationData":[OSD([subQ2,subQ1,subQ0])],"isStart":false})]}),makeQuery(id+"FbRMCi4XYvqGRgo_1.11.F2.opExtrude","CAP_FACE",FACE,{"disambiguationData":[OSD([subQ2,subQ1,subQ0])],"isStart":false})]}),makeQuery(id+"FbRMCi4XYvqGRgo_1.12.F2.opExtrude","CAP_FACE",FACE,{"disambiguationData":[OSD([subQ2,subQ1,subQ0])],"isStart":false})]}),makeQuery(id+"FbRMCi4XYvqGRgo_1.13.F2.opExtrude","CAP_FACE",FACE,{"disambiguationData":[OSD([subQ2,subQ1,subQ0])],"isStart":false})]}),makeQuery(id+"FbRMCi4XYvqGRgo_1.14.F2.opExtrude","CAP_FACE",FACE,{"disambiguationData":[OSD([subQ2,subQ1,subQ0])],"isStart":false})]}),makeQuery(id+"FbRMCi4XYvqGRgo_1.15.F2.opExtrude","CAP_FACE",FACE,{"disambiguationData":[OSD([subQ2,subQ1,subQ0])],"isStart":false})]}),makeQuery(id+"FbRMCi4XYvqGRgo_1.16.F2.opExtrude","CAP_FACE",FACE,{"disambiguationData":[OSD([subQ2,subQ1,subQ0])],"isStart":false})]}),makeQuery(id+"FbRMCi4XYvqGRgo_1.17.F2.opExtrude","CAP_FACE",FACE,{"disambiguationData":[OSD([subQ2,subQ1,subQ0])],"isStart":false})]}),makeQuery(id+"FbRMCi4XYvqGRgo_1.18.F2.opExtrude","CAP_FACE",FACE,{"disambiguationData":[OSD([subQ2,subQ1,subQ0])],"isStart":false})]}),makeQuery(id+"FbRMCi4XYvqGRgo_1.19.F2.opExtrude","CAP_FACE",FACE,{"disambiguationData":[OSD([subQ2,subQ1,subQ0])],"isStart":false})]}),makeQuery(id+"FbRMCi4XYvqGRgo_1.20.F2.opExtrude","CAP_FACE",FACE,{"disambiguationData":[OSD([subQ2,subQ1,subQ0])],"isStart":false})]}),makeQuery(id+"FbRMCi4XYvqGRgo_1.21.F2.opExtrude","CAP_FACE",FACE,{"disambiguationData":[OSD([subQ2,subQ1,subQ0])],"isStart":false})]}),makeQuery(id+"FbRMCi4XYvqGRgo_1.22.F2.opExtrude","CAP_FACE",FACE,{"disambiguationData":[OSD([subQ2,subQ1,subQ0])],"isStart":false})]}),makeQuery(id+"FbRMCi4XYvqGRgo_1.23.F2.opExtrude","CAP_FACE",FACE,{"disambiguationData":[OSD([subQ2,subQ1,subQ0])],"isStart":false})]}),makeQuery(id+"FbRMCi4XYvqGRgo_1.24.F2.opExtrude","CAP_FACE",FACE,{"disambiguationData":[OSD([subQ2,subQ1,subQ0])],"isStart":false})]}),makeQuery(id+"FbRMCi4XYvqGRgo_1.25.F2.opExtrude","CAP_FACE",FACE,{"disambiguationData":[OSD([subQ2,subQ1,subQ0])],"isStart":false})]}),makeQuery(id+"FbRMCi4XYvqGRgo_1.26.F2.opExtrude","CAP_FACE",FACE,{"disambiguationData":[OSD([subQ2,subQ1,subQ0])],"isStart":false})]}),makeQuery(id+"FbRMCi4XYvqGRgo_1.27.F2.opExtrude","CAP_FACE",FACE,{"disambiguationData":[OSD([subQ2,subQ1,subQ0])],"isStart":false})]}),makeQuery(id+"FbRMCi4XYvqGRgo_1.28.F2.opExtrude","CAP_FACE",FACE,{"disambiguationData":[OSD([subQ2,subQ1,subQ0])],"isStart":false})]}),makeQuery(id+"FbRMCi4XYvqGRgo_1.29.F2.opExtrude","CAP_FACE",FACE,{"disambiguationData":[OSD([subQ2,subQ1,subQ0])],"isStart":false})]}),makeQuery(id+"F12.opExtrude","CAP_FACE",FACE,{"disambiguationData":[OSD([sQuery(id+"F11.wireOp",EDGE,"E10.bottom"),sQuery(id+"F11.wireOp",EDGE,"E10.top"),sQuery(id+"F11.wireOp",EDGE,"E10.left"),sQuery(id+"F11.wireOp",EDGE,"E10.right"),sQuery(id+"F11.wireOp",EDGE,"E11.bottom"),sQuery(id+"F11.wireOp",EDGE,"E11.top"),sQuery(id+"F11.wireOp",EDGE,"E11.left"),sQuery(id+"F11.wireOp",EDGE,"E11.right")])],"isStart":false})]});}
            var sketch = newSketch(context, id + "F13", { "sketchPlane" : qUnion([Q0])});
            skCircle(sketch, "E12", {"center": v(0, 0) * mm, "radius": 2.5 * mm});
            skSolve(sketch);
        }
        {
            var Q0;
            Q0=makeQuery(id+"F13.imprint","IMPRINT",FACE,{"disambiguationData":[TD([[makeQuery(id+"F13.imprint","IMPRINT",EDGE,{"derivedFrom":sQuery(id+"F13.wireOp",EDGE,"E12")}),1.0]])]});
            var Q1;
            Q1=sQuery(id+"F13.wireOp",EDGE,"E12");
            extrude(context, id + "F14", {"entities" : qUnion([Q0]), "operationType" : NewBodyOperationType.REMOVE, "surfaceEntities" : qUnion([Q1]), "endBound" : BoundingType.THROUGH_ALL, "oppositeDirection" : true, "depth" : 25 * mm, "offsetDistance" : 25 * mm});
        }
        {
            var Q0;
            {var subQ0=sQuery(id+"F11.wireOp",EDGE,"E10.right");Q0=makeQuery(id+"F12.boolean.opBoolean","INTERSECT",EDGE,{"derivedFrom":[makeQuery(id+"F10.boolean.opBoolean","COPY",FACE,{"derivedFrom":makeQuery(id+"F10.opExtrude","SWEPT_FACE",FACE,{"disambiguationData":[OSD([sQuery(id+"F9.wireOp",EDGE,"E9")])]})}),makeQuery(id+"F12.opExtrude","SWEPT_FACE",FACE,{"disambiguationData":[OSD([subQ0]),TDD([makeQuery(id+"F11.imprint","IMPRINT",EDGE,{"disambiguationData":[TD([[makeQuery(id+"F11.imprint","INTERSECT",VERTEX,{"derivedFrom":[sQuery(id+"F11.wireOp",EDGE,"E10.bottom"),subQ0]}),-1.0]])],"derivedFrom":subQ0})])]})]});}
            var Q1;
            Q1=makeQuery(id+"F12.opExtrude","SWEPT_EDGE",EDGE,{"disambiguationData":[OSD([sQuery(id+"F11.wireOp",EDGE,"E10.right"),sQuery(id+"F11.wireOp",EDGE,"E11.top")])]});
            var Q2;
            Q2=makeQuery(id+"F12.opExtrude","SWEPT_EDGE",EDGE,{"disambiguationData":[OSD([sQuery(id+"F11.wireOp",EDGE,"E10.left"),sQuery(id+"F11.wireOp",EDGE,"E11.top")])]});
            var Q3;
            {var subQ0=sQuery(id+"F11.wireOp",EDGE,"E11.top");Q3=makeQuery(id+"F12.boolean.opBoolean","INTERSECT",EDGE,{"derivedFrom":[makeQuery(id+"F10.boolean.opBoolean","COPY",FACE,{"derivedFrom":makeQuery(id+"F10.opExtrude","SWEPT_FACE",FACE,{"disambiguationData":[OSD([sQuery(id+"F9.wireOp",EDGE,"E9")])]})}),makeQuery(id+"F12.opExtrude","SWEPT_FACE",FACE,{"disambiguationData":[OSD([subQ0]),TDD([makeQuery(id+"F11.imprint","IMPRINT",EDGE,{"disambiguationData":[TD([[makeQuery(id+"F11.imprint","INTERSECT",VERTEX,{"derivedFrom":[subQ0,sQuery(id+"F11.wireOp",EDGE,"E11.right")]}),1.0]])],"derivedFrom":subQ0})])]})]});}
            var Q4;
            {var subQ0=sQuery(id+"F11.wireOp",EDGE,"E10.right");Q4=makeQuery(id+"F12.boolean.opBoolean","INTERSECT",EDGE,{"derivedFrom":[makeQuery(id+"F10.boolean.opBoolean","COPY",FACE,{"derivedFrom":makeQuery(id+"F10.opExtrude","SWEPT_FACE",FACE,{"disambiguationData":[OSD([sQuery(id+"F9.wireOp",EDGE,"E9")])]})}),makeQuery(id+"F12.opExtrude","SWEPT_FACE",FACE,{"disambiguationData":[OSD([subQ0]),TDD([makeQuery(id+"F11.imprint","IMPRINT",EDGE,{"disambiguationData":[TD([[makeQuery(id+"F11.imprint","INTERSECT",VERTEX,{"derivedFrom":[sQuery(id+"F11.wireOp",EDGE,"E10.top"),subQ0]}),1.0]])],"derivedFrom":subQ0})])]})]});}
            var Q5;
            {var subQ0=sQuery(id+"F11.wireOp",EDGE,"E11.top");Q5=makeQuery(id+"F12.boolean.opBoolean","INTERSECT",EDGE,{"derivedFrom":[makeQuery(id+"F10.boolean.opBoolean","COPY",FACE,{"derivedFrom":makeQuery(id+"F10.opExtrude","SWEPT_FACE",FACE,{"disambiguationData":[OSD([sQuery(id+"F9.wireOp",EDGE,"E9")])]})}),makeQuery(id+"F12.opExtrude","SWEPT_FACE",FACE,{"disambiguationData":[OSD([subQ0]),TDD([makeQuery(id+"F11.imprint","IMPRINT",EDGE,{"disambiguationData":[TD([[makeQuery(id+"F11.imprint","INTERSECT",VERTEX,{"derivedFrom":[subQ0,sQuery(id+"F11.wireOp",EDGE,"E11.left")]}),-1.0]])],"derivedFrom":subQ0})])]})]});}
            var Q6;
            {var subQ0=sQuery(id+"F11.wireOp",EDGE,"E10.left");Q6=makeQuery(id+"F12.boolean.opBoolean","INTERSECT",EDGE,{"derivedFrom":[makeQuery(id+"F10.boolean.opBoolean","COPY",FACE,{"derivedFrom":makeQuery(id+"F10.opExtrude","SWEPT_FACE",FACE,{"disambiguationData":[OSD([sQuery(id+"F9.wireOp",EDGE,"E9")])]})}),makeQuery(id+"F12.opExtrude","SWEPT_FACE",FACE,{"disambiguationData":[OSD([subQ0]),TDD([makeQuery(id+"F11.imprint","IMPRINT",EDGE,{"disambiguationData":[TD([[makeQuery(id+"F11.imprint","INTERSECT",VERTEX,{"derivedFrom":[sQuery(id+"F11.wireOp",EDGE,"E10.top"),subQ0]}),1.0]])],"derivedFrom":subQ0})])]})]});}
            var Q7;
            Q7=makeQuery(id+"F12.opExtrude","SWEPT_EDGE",EDGE,{"disambiguationData":[OSD([sQuery(id+"F11.wireOp",EDGE,"E10.left"),sQuery(id+"F11.wireOp",EDGE,"E11.bottom")])]});
            var Q8;
            Q8=makeQuery(id+"F12.opExtrude","SWEPT_EDGE",EDGE,{"disambiguationData":[OSD([sQuery(id+"F11.wireOp",EDGE,"E10.right"),sQuery(id+"F11.wireOp",EDGE,"E11.bottom")])]});
            var Q9;
            {var subQ0=sQuery(id+"F11.wireOp",EDGE,"E11.bottom");Q9=makeQuery(id+"F12.boolean.opBoolean","INTERSECT",EDGE,{"derivedFrom":[makeQuery(id+"F10.boolean.opBoolean","COPY",FACE,{"derivedFrom":makeQuery(id+"F10.opExtrude","SWEPT_FACE",FACE,{"disambiguationData":[OSD([sQuery(id+"F9.wireOp",EDGE,"E9")])]})}),makeQuery(id+"F12.opExtrude","SWEPT_FACE",FACE,{"disambiguationData":[OSD([subQ0]),TDD([makeQuery(id+"F11.imprint","IMPRINT",EDGE,{"disambiguationData":[TD([[makeQuery(id+"F11.imprint","INTERSECT",VERTEX,{"derivedFrom":[subQ0,sQuery(id+"F11.wireOp",EDGE,"E11.left")]}),-1.0]])],"derivedFrom":subQ0})])]})]});}
            var Q10;
            {var subQ0=sQuery(id+"F11.wireOp",EDGE,"E10.left");Q10=makeQuery(id+"F12.boolean.opBoolean","INTERSECT",EDGE,{"derivedFrom":[makeQuery(id+"F10.boolean.opBoolean","COPY",FACE,{"derivedFrom":makeQuery(id+"F10.opExtrude","SWEPT_FACE",FACE,{"disambiguationData":[OSD([sQuery(id+"F9.wireOp",EDGE,"E9")])]})}),makeQuery(id+"F12.opExtrude","SWEPT_FACE",FACE,{"disambiguationData":[OSD([subQ0]),TDD([makeQuery(id+"F11.imprint","IMPRINT",EDGE,{"disambiguationData":[TD([[makeQuery(id+"F11.imprint","INTERSECT",VERTEX,{"derivedFrom":[sQuery(id+"F11.wireOp",EDGE,"E10.bottom"),subQ0]}),-1.0]])],"derivedFrom":subQ0})])]})]});}
            var Q11;
            {var subQ0=sQuery(id+"F11.wireOp",EDGE,"E11.bottom");Q11=makeQuery(id+"F12.boolean.opBoolean","INTERSECT",EDGE,{"derivedFrom":[makeQuery(id+"F10.boolean.opBoolean","COPY",FACE,{"derivedFrom":makeQuery(id+"F10.opExtrude","SWEPT_FACE",FACE,{"disambiguationData":[OSD([sQuery(id+"F9.wireOp",EDGE,"E9")])]})}),makeQuery(id+"F12.opExtrude","SWEPT_FACE",FACE,{"disambiguationData":[OSD([subQ0]),TDD([makeQuery(id+"F11.imprint","IMPRINT",EDGE,{"disambiguationData":[TD([[makeQuery(id+"F11.imprint","INTERSECT",VERTEX,{"derivedFrom":[subQ0,sQuery(id+"F11.wireOp",EDGE,"E11.right")]}),1.0]])],"derivedFrom":subQ0})])]})]});}
            fillet(context, id + "F15", {"entities" : qUnion([Q0, Q1, Q2, Q3, Q4, Q5, Q6, Q7, Q8, Q9, Q10, Q11]), "radius" : 3 * mm, "tangentPropagation" : true, "allowEdgeOverflow" : false});
        }
        {
            var Q0;
            Q0=qCreatedBy(makeId("Top.planeOp"),FACE);
            var sketch = newSketch(context, id + "F16", { "sketchPlane" : qUnion([Q0])});
            skLineSegment(sketch, "E13.bottom", {"start": v(-28.7, -19) * mm, "end": v(4.5, -19) * mm});
            skLineSegment(sketch, "E13.top", {"start": v(-28.7, 4.5) * mm, "end": v(4.5, 4.5) * mm});
            skLineSegment(sketch, "E13.left", {"start": v(-28.7, -19) * mm, "end": v(-28.7, 4.5) * mm});
            skLineSegment(sketch, "E13.right", {"start": v(4.5, -19) * mm, "end": v(4.5, 4.5) * mm});
            skSolve(sketch);
        }
        {
            var Q0;
            Q0 = qSketchRegion(id + "F16", true);
            extrude(context, id + "F17", {"entities" : qUnion([Q0]), "oppositeDirection" : true, "depth" : 3 * mm, "offsetDistance" : 25 * mm});
        }
        {
            var Q0;
            Q0=makeQuery(id+"F17.opExtrude","CAP_FACE",FACE,{"disambiguationData":[OSD([sQuery(id+"F16.wireOp",EDGE,"E13.bottom"),sQuery(id+"F16.wireOp",EDGE,"E13.top"),sQuery(id+"F16.wireOp",EDGE,"E13.left"),sQuery(id+"F16.wireOp",EDGE,"E13.right")])],"isStart":true});
            var sketch = newSketch(context, id + "F18", { "sketchPlane" : qUnion([Q0])});
            skLineSegment(sketch, "E14.0", {"start": v(-25.35, 0.65) * mm, "end": v(-25.35, -13.35) * mm});
            skLineSegment(sketch, "E14.1", {"start": v(-24.05, 0.65) * mm, "end": v(-25.35, 0.65) * mm});
            skLineSegment(sketch, "E14.2", {"start": v(-24.05, 0.65) * mm, "end": v(-24.05, -13.35) * mm});
            skLineSegment(sketch, "E15", {"start": v(-25.35, -13.35) * mm, "end": v(-24.05, -13.35) * mm});
            skSolve(sketch);
        }
        {
            var Q0;
            Q0=makeQuery(id+"F18.imprint","IMPRINT",FACE,{"disambiguationData":[TD([[makeQuery(id+"F18.imprint","IMPRINT",EDGE,{"derivedFrom":sQuery(id+"F18.wireOp",EDGE,"E14.0")}),1.0]])]});
            extrude(context, id + "F19", {"entities" : qUnion([Q0]), "operationType" : NewBodyOperationType.ADD, "depth" : 5 * mm, "offsetDistance" : 25 * mm});
        }
        {
            var Q0;
            Q0=makeQuery(id+"F17.opExtrude","SWEPT_EDGE",EDGE,{"disambiguationData":[OSD([sQuery(id+"F16.wireOp",EDGE,"E13.bottom"),sQuery(id+"F16.wireOp",EDGE,"E13.right")])]});
            var Q1;
            Q1=makeQuery(id+"F17.opExtrude","SWEPT_EDGE",EDGE,{"disambiguationData":[OSD([sQuery(id+"F16.wireOp",EDGE,"E13.top"),sQuery(id+"F16.wireOp",EDGE,"E13.right")])]});
            var Q2;
            Q2=makeQuery(id+"F17.opExtrude","SWEPT_EDGE",EDGE,{"disambiguationData":[OSD([sQuery(id+"F16.wireOp",EDGE,"E13.top"),sQuery(id+"F16.wireOp",EDGE,"E13.left")])]});
            var Q3;
            Q3=makeQuery(id+"F17.opExtrude","SWEPT_EDGE",EDGE,{"disambiguationData":[OSD([sQuery(id+"F16.wireOp",EDGE,"E13.bottom"),sQuery(id+"F16.wireOp",EDGE,"E13.left")])]});
            fillet(context, id + "F20", {"entities" : qUnion([Q0, Q1, Q2, Q3]), "radius" : 5 * mm, "tangentPropagation" : true, "allowEdgeOverflow" : false});
        }
        {
            var Q0;
            Q0=makeQuery(id+"F17.opExtrude","CAP_FACE",FACE,{"disambiguationData":[OSD([sQuery(id+"F16.wireOp",EDGE,"E13.bottom"),sQuery(id+"F16.wireOp",EDGE,"E13.top"),sQuery(id+"F16.wireOp",EDGE,"E13.left"),sQuery(id+"F16.wireOp",EDGE,"E13.right")])],"isStart":true});
            var sketch = newSketch(context, id + "F21", { "sketchPlane" : qUnion([Q0])});
            skCircle(sketch, "E16.0", {"center": v(0, 0) * mm, "radius": 2.15 * mm});
            skSolve(sketch);
        }
        {
            var Q0;
            Q0=makeQuery(id+"F21.imprint","IMPRINT",FACE,{"disambiguationData":[TD([[makeQuery(id+"F21.imprint","IMPRINT",EDGE,{"derivedFrom":sQuery(id+"F21.wireOp",EDGE,"E16.0")}),1.0]])]});
            extrude(context, id + "F22", {"entities" : qUnion([Q0]), "operationType" : NewBodyOperationType.ADD, "depth" : 5 * mm, "offsetDistance" : 25 * mm});
        }
        {
            var Q0;
            Q0=makeQuery(id+"F22.opExtrude","CAP_FACE",FACE,{"disambiguationData":[OSD([sQuery(id+"F21.wireOp",EDGE,"E16.0")])],"isStart":false});
            var sketch = newSketch(context, id + "F23", { "sketchPlane" : qUnion([Q0])});
            skCircle(sketch, "E17.0", {"center": v(0, 0) * mm, "radius": 2.3 * mm});
            skCircle(sketch, "E18.0", {"center": v(0, 0) * mm, "radius": 3.8 * mm});
            skSolve(sketch);
        }
        {
            var Q0;
            Q0=makeQuery(id+"F23.imprint","IMPRINT",FACE,{"disambiguationData":[TD([[makeQuery(id+"F23.imprint","IMPRINT",EDGE,{"derivedFrom":sQuery(id+"F23.wireOp",EDGE,"E17.0")}),-1.0]])]});
            extrude(context, id + "F24", {"entities" : qUnion([Q0]), "oppositeDirection" : true, "depth" : 1.8 * mm, "offsetDistance" : 25 * mm});
        }
        {
            var Q0;
            Q0=makeQuery(id+"F24.opExtrude","CAP_FACE",FACE,{"disambiguationData":[OSD([sQuery(id+"F23.wireOp",EDGE,"E17.0"),sQuery(id+"F23.wireOp",EDGE,"E18.0")])],"isStart":true});
            var sketch = newSketch(context, id + "F25", { "sketchPlane" : qUnion([Q0])});
            skCircle(sketch, "E19.0", {"center": v(0, 0) * mm, "radius": 3.8 * mm});
            skSolve(sketch);
        }
        {
            var Q0;
            Q0 = qSketchRegion(id + "F25", true);
            extrude(context, id + "F26", {"entities" : qUnion([Q0]), "operationType" : NewBodyOperationType.ADD, "depth" : 1 * mm, "offsetDistance" : 25 * mm});
        }
        {
            var Q0;
            Q0=makeQuery(id+"F19.opExtrude","CAP_FACE",FACE,{"disambiguationData":[OSD([sQuery(id+"F18.wireOp",EDGE,"E14.0"),sQuery(id+"F18.wireOp",EDGE,"E14.1"),sQuery(id+"F18.wireOp",EDGE,"E14.2"),sQuery(id+"F18.wireOp",EDGE,"E15")])],"isStart":false});
            var sketch = newSketch(context, id + "F27", { "sketchPlane" : qUnion([Q0])});
            skLineSegment(sketch, "E20.0", {"start": v(-25.5, 0.8) * mm, "end": v(-25.5, -13.5) * mm});
            skLineSegment(sketch, "E20.1", {"start": v(-23.9, 0.8) * mm, "end": v(-25.5, 0.8) * mm});
            skLineSegment(sketch, "E20.2", {"start": v(-23.9, 0.8) * mm, "end": v(-23.9, -13.5) * mm});
            skLineSegment(sketch, "E20.3", {"start": v(-25.5, -13.5) * mm, "end": v(-23.9, -13.5) * mm});
            skLineSegment(sketch, "E21.0", {"start": v(-27, 2.3) * mm, "end": v(-27, -15) * mm});
            skLineSegment(sketch, "E21.1", {"start": v(-22.4, 2.3) * mm, "end": v(-27, 2.3) * mm});
            skLineSegment(sketch, "E21.2", {"start": v(-22.4, 2.3) * mm, "end": v(-22.4, -15) * mm});
            skLineSegment(sketch, "E21.3", {"start": v(-27, -15) * mm, "end": v(-22.4, -15) * mm});
            skSolve(sketch);
        }
        {
            var Q0;
            Q0=makeQuery(id+"F27.imprint","IMPRINT",FACE,{"disambiguationData":[TD([[makeQuery(id+"F27.imprint","IMPRINT",EDGE,{"derivedFrom":sQuery(id+"F27.wireOp",EDGE,"E20.0")}),-1.0]])]});
            extrude(context, id + "F28", {"entities" : qUnion([Q0]), "oppositeDirection" : true, "depth" : 1.8 * mm, "offsetDistance" : 25 * mm});
        }
        {
            var Q0;
            Q0=makeQuery(id+"F28.opExtrude","CAP_FACE",FACE,{"disambiguationData":[OSD([sQuery(id+"F27.wireOp",EDGE,"E20.0"),sQuery(id+"F27.wireOp",EDGE,"E20.1"),sQuery(id+"F27.wireOp",EDGE,"E20.2"),sQuery(id+"F27.wireOp",EDGE,"E20.3"),sQuery(id+"F27.wireOp",EDGE,"E21.0"),sQuery(id+"F27.wireOp",EDGE,"E21.1"),sQuery(id+"F27.wireOp",EDGE,"E21.2"),sQuery(id+"F27.wireOp",EDGE,"E21.3")])],"isStart":true});
            var sketch = newSketch(context, id + "F29", { "sketchPlane" : qUnion([Q0])});
            skLineSegment(sketch, "E22.0", {"start": v(-22.4, 2.3) * mm, "end": v(-22.4, -15) * mm});
            skLineSegment(sketch, "E22.1", {"start": v(-27, -15) * mm, "end": v(-22.4, -15) * mm});
            skLineSegment(sketch, "E22.2", {"start": v(-27, 2.3) * mm, "end": v(-27, -15) * mm});
            skLineSegment(sketch, "E23.0", {"start": v(-22.4, 2.3) * mm, "end": v(-27, 2.3) * mm});
            skSolve(sketch);
        }
        {
            var Q0;
            Q0 = qSketchRegion(id + "F29", true);
            extrude(context, id + "F30", {"entities" : qUnion([Q0]), "operationType" : NewBodyOperationType.ADD, "depth" : 1 * mm, "offsetDistance" : 25 * mm});
        }
        {
            var Q0;
            Q0=qCreatedBy(makeId("Top.planeOp"),FACE);
            var sketch = newSketch(context, id + "F31", { "sketchPlane" : qUnion([Q0])});
            skLineSegment(sketch, "E24", {"start": v(-26.7, -49.44) * mm, "end": v(-29.7, -54.98) * mm});
            skLineSegment(sketch, "E25", {"start": v(-29.7, -54.98) * mm, "end": v(-26.7, -53.48) * mm});
            skLineSegment(sketch, "E26", {"start": v(-26.7, -49.44) * mm, "end": v(-26.7, -53.48) * mm});
            skSolve(sketch);
        }
        {
            var Q0;
            Q0=makeQuery(id+"F31.imprint","IMPRINT",FACE,{"disambiguationData":[TD([[makeQuery(id+"F31.imprint","IMPRINT",EDGE,{"derivedFrom":sQuery(id+"F31.wireOp",EDGE,"E24")}),1.0]])]});
            extrude(context, id + "F32", {"entities" : qUnion([Q0]), "operationType" : NewBodyOperationType.ADD, "depth" : 3 * mm, "offsetDistance" : 25 * mm});
        }
        {
            var Q0;
            Q0=qCreatedBy(makeId("Top.planeOp"),FACE);
            var sketch = newSketch(context, id + "F33", { "sketchPlane" : qUnion([Q0])});
            skLineSegment(sketch, "E27.bottom", {"start": v(-30.7, -0.5) * mm, "end": v(-32.2, -0.5) * mm});
            skLineSegment(sketch, "E27.top", {"start": v(-28.7, -3.5) * mm, "end": v(-32.2, -3.5) * mm});
            skLineSegment(sketch, "E27.left", {"start": v(-28.7, -2) * mm, "end": v(-28.7, -3.5) * mm});
            skLineSegment(sketch, "E27.right", {"start": v(-32.2, -0.5) * mm, "end": v(-32.2, -3.5) * mm});
            skLineSegment(sketch, "E28", {"start": v(-30.7, -0.5) * mm, "end": v(-30.7, -2) * mm});
            skLineSegment(sketch, "E29", {"start": v(-30.7, -2) * mm, "end": v(-28.7, -2) * mm});
            skPoint(sketch, "E30.orphan", {"position": v(-28.7, -0.5) * mm});
            skSolve(sketch);
        }
        {
            var Q0;
            Q0=makeQuery(id+"F33.imprint","IMPRINT",FACE,{"disambiguationData":[TD([[makeQuery(id+"F33.imprint","IMPRINT",EDGE,{"derivedFrom":sQuery(id+"F33.wireOp",EDGE,"E27.bottom")}),1.0]])]});
            extrude(context, id + "F34", {"entities" : qUnion([Q0]), "operationType" : NewBodyOperationType.ADD, "oppositeDirection" : true, "depth" : 3 * mm, "offsetDistance" : 25 * mm});
        }
        {
            var Q0;
            Q0=makeQuery(id+"F34.boolean.opBoolean","MERGE",FACE,{"derivedFrom":[makeQuery(id+"F17.opExtrude","CAP_FACE",FACE,{"disambiguationData":[OSD([sQuery(id+"F16.wireOp",EDGE,"E13.bottom"),sQuery(id+"F16.wireOp",EDGE,"E13.top"),sQuery(id+"F16.wireOp",EDGE,"E13.left"),sQuery(id+"F16.wireOp",EDGE,"E13.right")])],"isStart":true}),makeQuery(id+"F34.opExtrude","CAP_FACE",FACE,{"disambiguationData":[OSD([sQuery(id+"F33.wireOp",EDGE,"E27.bottom"),sQuery(id+"F33.wireOp",EDGE,"E27.top"),sQuery(id+"F33.wireOp",EDGE,"E27.left"),sQuery(id+"F33.wireOp",EDGE,"E27.right"),sQuery(id+"F33.wireOp",EDGE,"E28"),sQuery(id+"F33.wireOp",EDGE,"E29")])],"isStart":true})]});
            var sketch = newSketch(context, id + "F35", { "sketchPlane" : qUnion([Q0])});
            skLineSegment(sketch, "E31.bottom", {"start": v(-28.1, -14) * mm, "end": v(-27.1, -14) * mm});
            skLineSegment(sketch, "E31.top", {"start": v(-28.1, -13) * mm, "end": v(-27.1, -13) * mm});
            skLineSegment(sketch, "E31.left", {"start": v(-28.1, -14) * mm, "end": v(-28.1, -13) * mm});
            skLineSegment(sketch, "E31.right", {"start": v(-27.1, -14) * mm, "end": v(-27.1, -13) * mm});
            skSolve(sketch);
        }
        {
            var Q0;
            Q0=makeQuery(id+"F35.imprint","IMPRINT",FACE,{"disambiguationData":[TD([[makeQuery(id+"F35.imprint","IMPRINT",EDGE,{"derivedFrom":sQuery(id+"F35.wireOp",EDGE,"E31.bottom")}),1.0]])]});
            extrude(context, id + "F36", {"entities" : qUnion([Q0]), "operationType" : NewBodyOperationType.ADD, "depth" : 1 * mm, "offsetDistance" : 25 * mm});
        }
    });
